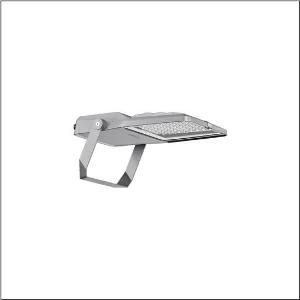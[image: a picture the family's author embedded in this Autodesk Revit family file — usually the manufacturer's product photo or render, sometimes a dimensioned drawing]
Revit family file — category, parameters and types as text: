
# Revit family: floodlight_fl_21_iq_mini___pl43_5xa7772c1a1a_56dc
name_source: partatom
category: Lighting Fixtures
units: mm (PartAtom-declared; Revit-internal decimal feet)

## family parameters
Cut with Voids When Loaded = No
Host = Face
Light Source = No
Part Type = Normal
Room Calculation Point = No
Round Connector Dimension = Use Diameter
Shared = No

## types (1)
- --- (1 x LED, 10370 lm, 87.2 W, 2200K)
    Apparent Load = 87 VA
    CIE Flux Codes = 27 78 99 100 100
    Color Rendering = 70
    Color Temperature = 2200K
    Default Elevation = 1800 mm
    Description = Floodlight FL 21 iQ mini, floodlight, primary light control with lens, of PMMA, primary optical cover: protective disc, of toughened safety glass, transparent, light distribution: PL43, light emission: direct distribution, installation type: surface-mounted, LED, High Power LED, rated luminous flux: 10.370lm, luminous efficacy: 119lm/W, light colour: 722, colour temperature: 2200K, control: Street-Remote, Auto-Match, Temp-Guard, Night-Set, Smart-Wire, Desk-Remote (wireless, voltage-free reading and setting of iQ features in the workshop via application-optimized NFC function/RFID function), optimised constant luminous flux control (CLO 2.0), with terminal, 6-pole, mains connection: 220..240V, AC, 50/60Hz, start of lifetime: 87W, end of service life: 92W, reduction: 40W, luminaire housing, of diecast aluminium, powder-coated, Siteco® metallic grey (DB 702S), corrosivity category C5 mid according to DIN EN ISO 12944, sealing non-destructively replaceable, mounting bracket, of steel, galvanised, powder-coated, Siteco® metallic grey (DB 702S), protection rating (complete): IP66, insulation class (complete): insulation class II (safety insulation), certification: CE, ENEC, VDE, protection symbol: D, impact resistance: IK08, permissible operating ambient temperature: -40..+40°C, permissible operating ambient temperature for outdoor applications: -40..+50°C, standard: DIN EN 12944, LABS conformity tested according to VDMA 24364:2018-05, packaging unit: 1 piece

Light Distribution: PL43
    Height = 70 mm
    Lamp = 1 x LED
    Lamp Light Flux = 10370 lm
    Lamp Power = 87.2 W
    Lamp count = 1
    Length = 485 mm
    Luminous efficacy = 119 lm/W
    Manufacturer = Siteco
    ModVariant = No
    Model = 5XA7772C1A1A
    Number of Poles = 1
    OnlyDefault = Yes
    Power Factor = 1
    Product Name = Floodlight FL 21 iQ mini | PL43
    Product group = floodlight | pylon annexe
    ProductGroupID = 6200
    Protection Class = Protection class II
    Protection Degree = IP 66
    RLX_Detail_Level = 1
    RLX_Emergency_Light_Flux = 0 lm
    RLX_Emergency_Type = 0
    RLX_Emergency_Type_DB = No
    RlxData = <blob elided: 96077 chars, md5=36c4cc3c>
    Socket = socket
    Standby Power = 0 W
    System Light Flux = 10370 lm
    System Power = 87 W
    Type Comments = factory setting: luminous flux: 100 % | dim-lin: 254 | 456 mA
    Type Image = l_1006845.jpg
    URL = http://relux.com
    VarID = @adj_112545
    Voltage = 0 V
    Weight = 0.00 kg
    Width = 337 mm

## geometry (parser evidence)
native form markers: Blend x4, Sweep x13
no freeform markers — native parametric forms only
